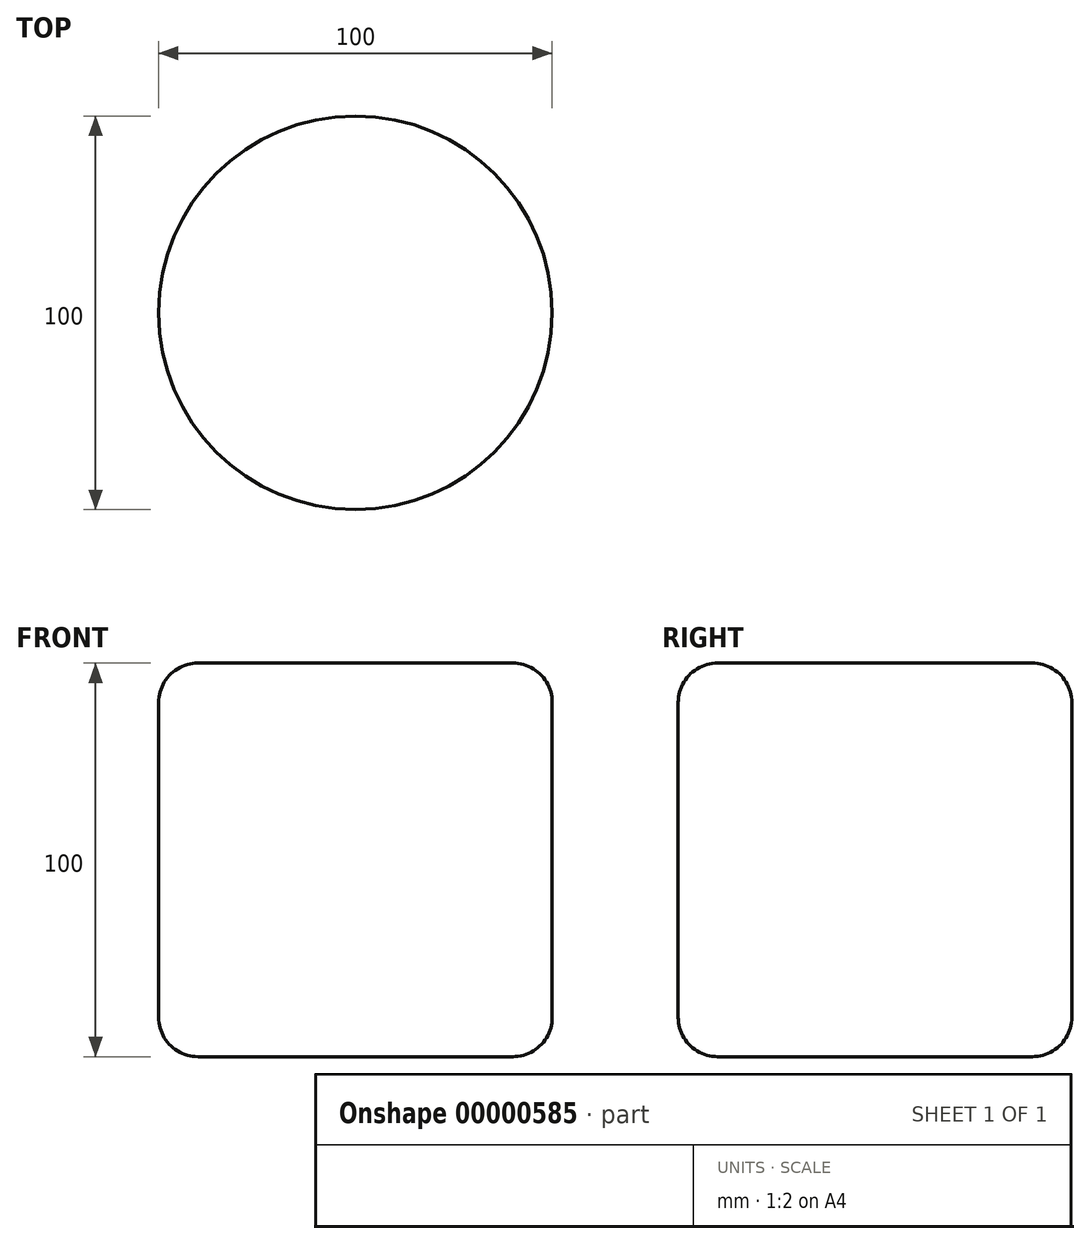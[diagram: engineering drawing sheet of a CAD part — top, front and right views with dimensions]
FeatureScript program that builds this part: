
annotation { "Feature Type Name" : "Feature", "Feature Type Description" : "" }
export const myFeature = defineFeature(function(context is Context, id is Id, definition is map)
    precondition{}
    {
        {
            var Q0;
            Q0=qCreatedBy(makeId("Top.planeOp"),FACE);
            var sketch = newSketch(context, id + "F0", { "sketchPlane" : qUnion([Q0])});
            skCircle(sketch, "E0", {"center": v(0, 0) * mm, "radius": 50 * mm});
            skSolve(sketch);
        }
        {
            var Q0;
            Q0=makeQuery(id+"F0.imprint","IMPRINT",FACE,{"disambiguationData":[TD([[makeQuery(id+"F0.imprint","IMPRINT",EDGE,{"derivedFrom":sQuery(id+"F0.wireOp",EDGE,"E0")}),1.0]])]});
            var Q1;
            Q1=sQuery(id+"F0.wireOp",EDGE,"E0");
            extrude(context, id + "F1", {"entities" : qUnion([Q0]), "surfaceEntities" : qUnion([Q1]), "depth" : 100 * mm});
        }
        {
            var Q0;
            Q0=makeQuery(id+"F1.opExtrude","CAP_EDGE",EDGE,{"disambiguationData":[OSD([sQuery(id+"F0.wireOp",EDGE,"E0")])],"isStart":false});
            var Q1;
            Q1=makeQuery(id+"F1.opExtrude","CAP_EDGE",EDGE,{"disambiguationData":[OSD([sQuery(id+"F0.wireOp",EDGE,"E0")])],"isStart":true});
            fillet(context, id + "F2", {"entities" : qUnion([Q0, Q1]), "radius" : 10 * mm, "tangentPropagation" : true, "allowEdgeOverflow" : false});
        }
    });
